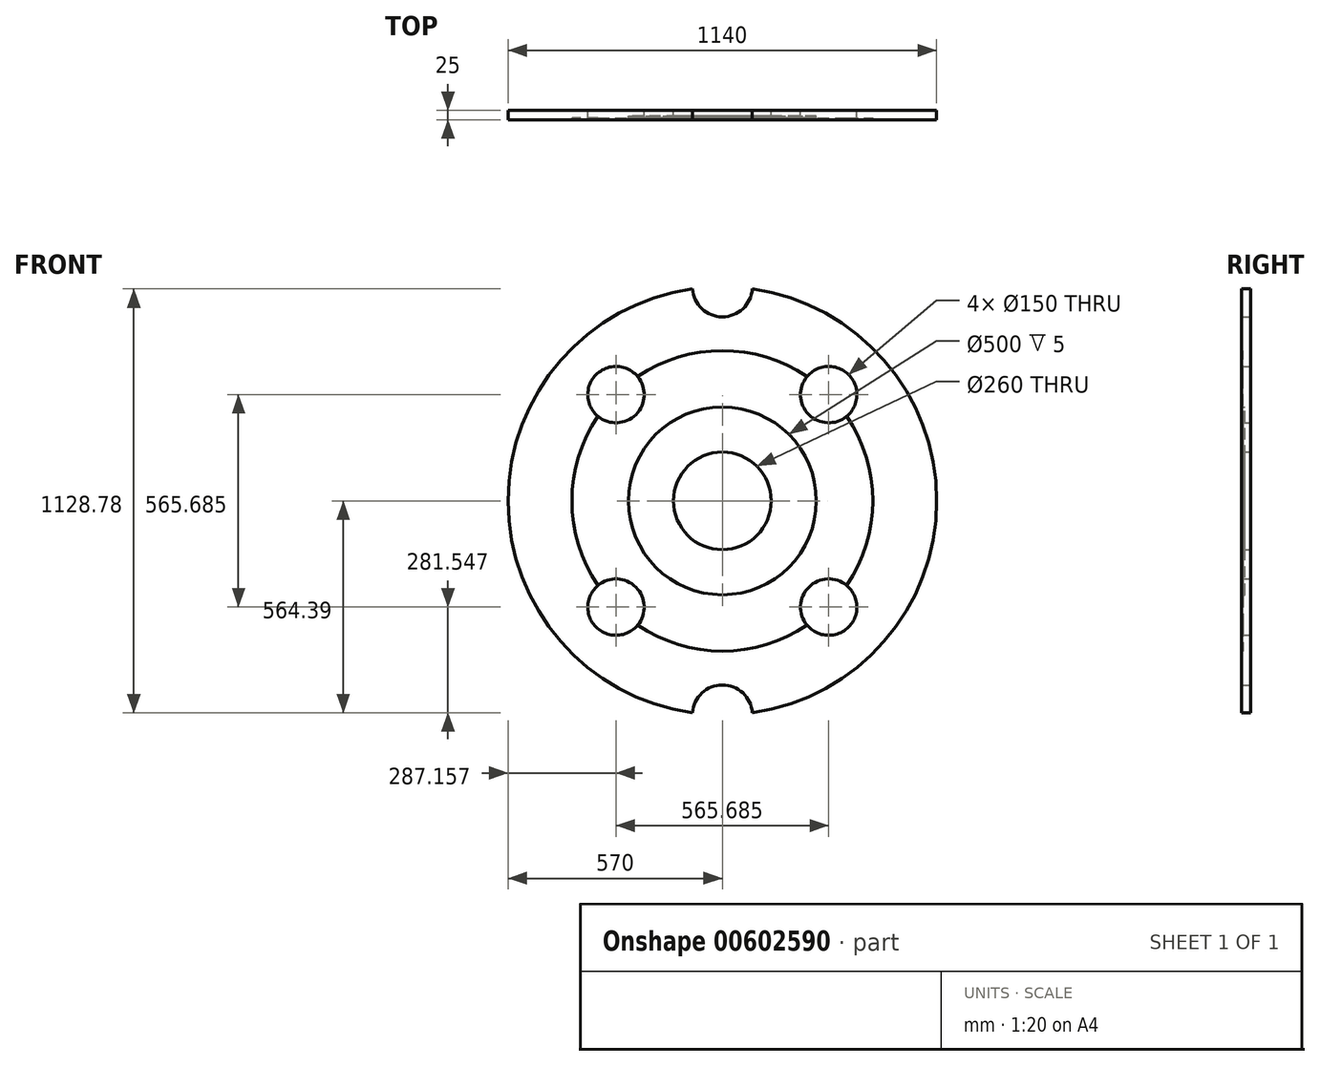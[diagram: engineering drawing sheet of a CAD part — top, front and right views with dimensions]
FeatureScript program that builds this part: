
annotation { "Feature Type Name" : "Feature", "Feature Type Description" : "" }
export const myFeature = defineFeature(function(context is Context, id is Id, definition is map)
    precondition{}
    {
        {
            var Q0;
            Q0=qCreatedBy(makeId("Front.planeOp"),FACE);
            var sketch = newSketch(context, id + "F0", { "sketchPlane" : qUnion([Q0])});
            skCircle(sketch, "E0", {"center": v(0, 0) * mm, "radius": 130 * mm});
            skCircle(sketch, "E1", {"center": v(0, 0) * mm, "radius": 200 * mm, "construction": true});
            skCircle(sketch, "E2", {"center": v(0, 0) * mm, "radius": 250 * mm});
            skArc(sketch, "E3", {"start": v(-79.8, 564.39) * mm, "mid": v(-570, 0) * mm, "end": v(-79.8, -564.39) * mm});
            skCircle(sketch, "E4", {"center": v(-282.84, 282.84) * mm, "radius": 75 * mm});
            skCircle(sketch, "E5", {"center": v(-282.84, -282.84) * mm, "radius": 75 * mm});
            skCircle(sketch, "E6", {"center": v(282.84, -282.84) * mm, "radius": 75 * mm});
            skCircle(sketch, "E7", {"center": v(282.84, 282.84) * mm, "radius": 75 * mm});
            skLineSegment(sketch, "E8", {"start": v(0, 0) * mm, "end": v(-282.84, 282.84) * mm, "construction": true});
            skLineSegment(sketch, "E9", {"start": v(0, 0) * mm, "end": v(282.84, 282.84) * mm, "construction": true});
            skLineSegment(sketch, "E10", {"start": v(0, 0) * mm, "end": v(282.84, -282.84) * mm, "construction": true});
            skLineSegment(sketch, "E11", {"start": v(0, 0) * mm, "end": v(-282.84, -282.84) * mm, "construction": true});
            skLineSegment(sketch, "E12", {"start": v(0, 0) * mm, "end": v(-570, 0) * mm, "construction": true});
            skArc(sketch, "E13", {"start": v(-330.67, 225.07) * mm, "mid": v(-400, 0) * mm, "end": v(-330.67, -225.07) * mm});
            skArc(sketch, "E14.trimOffspring", {"start": v(225.07, 330.67) * mm, "mid": v(0, 400) * mm, "end": v(-225.07, 330.67) * mm});
            skArc(sketch, "E15.trimOffspring", {"start": v(330.67, -225.07) * mm, "mid": v(400, 0) * mm, "end": v(330.67, 225.07) * mm});
            skArc(sketch, "E16.trimOffspring", {"start": v(-225.07, -330.67) * mm, "mid": v(0, -400) * mm, "end": v(225.07, -330.67) * mm});
            skLineSegment(sketch, "E17", {"start": v(0, 570) * mm, "end": v(0, -570) * mm, "construction": true});
            skArc(sketch, "E18", {"start": v(-79.8, 564.39) * mm, "mid": v(0, 490) * mm, "end": v(79.8, 564.39) * mm});
            skArc(sketch, "E19", {"start": v(79.8, -564.39) * mm, "mid": v(0, -490) * mm, "end": v(-79.8, -564.39) * mm});
            skArc(sketch, "E20.trimOffspring", {"start": v(79.8, -564.39) * mm, "mid": v(570, 0) * mm, "end": v(79.8, 564.39) * mm});
            skSolve(sketch);
        }
        {
            var Q0;
            Q0=makeQuery(id+"F0.imprint","IMPRINT",FACE,{"disambiguationData":[TD([[makeQuery(id+"F0.imprint","IMPRINT",EDGE,{"derivedFrom":sQuery(id+"F0.wireOp",EDGE,"E3")}),1.0]])]});
            extrude(context, id + "F1", {"entities" : qUnion([Q0]), "depth" : 25 * mm, "offsetDistance" : 25 * mm});
        }
        {
            var Q0;
            Q0=makeQuery(id+"F0.imprint","IMPRINT",FACE,{"disambiguationData":[TD([[makeQuery(id+"F0.imprint","IMPRINT",EDGE,{"derivedFrom":sQuery(id+"F0.wireOp",EDGE,"E2")}),-1.0]])]});
            extrude(context, id + "F2", {"entities" : qUnion([Q0]), "operationType" : NewBodyOperationType.ADD, "depth" : 20 * mm, "offsetDistance" : 25 * mm});
        }
        {
            var Q0;
            Q0=makeQuery(id+"F0.imprint","IMPRINT",FACE,{"disambiguationData":[TD([[makeQuery(id+"F0.imprint","IMPRINT",EDGE,{"derivedFrom":sQuery(id+"F0.wireOp",EDGE,"E0")}),-1.0]])]});
            extrude(context, id + "F3", {"entities" : qUnion([Q0]), "operationType" : NewBodyOperationType.ADD, "depth" : 15 * mm, "offsetDistance" : 25 * mm});
        }
    });
